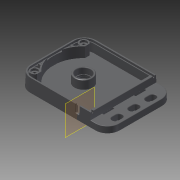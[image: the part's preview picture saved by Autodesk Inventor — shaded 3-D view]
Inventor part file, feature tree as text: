
AUTODESK INVENTOR PART (.ipt)
format: ipt  version: 2013 (Build 170138000, 138)  size: 991,744 bytes
history: native  units: mm
features: extrude x19, sketch x15, fillet x11, plane x4, hole x2, projected_geometry x1
ambient origin geometry x8: Origin, YZ Plane, XZ Plane, XY Plane, X Axis, Y Axis, Z Axis, Center Point
bodies: Solid1 (feature_tree)
feature tree (52):
  extrude  "Extrusion1"  TaperAngle=0.0deg  [1 undecoded]
  plane  "Work Plane1"
  extrude  "Extrusion2"  Depth=15.882496mm
  fillet  "Fillet1"  Radius=13.081mm
  plane  "Work Plane2"
  sketch  "Sketch5"  dims[d6=9.4996mm d7=0.0mm d8=-1.4986mm d9=8.9916mm]
  extrude  "Extrusion3"  Depth=8.9916mm
  extrude  "Extrusion4"  Depth=0.6096mm
  sketch  "Sketch9"  dims[d10=8.6614mm d12=0.6096mm d13=0.993147mm]
  sketch  "Sketch10"  dims[d14=0.6096mm d15=0.6096mm]
  extrude  "Extrusion10"  Depth=0.6096mm
  extrude  "Extrusion11"  Depth=7.668253mm
  extrude  "Extrusion12"  Depth=7.054107mm
  extrude  "Extrusion13"  Depth=6.1976mm
  hole  "Hole1"  [1 undecoded]
  plane  "Work Plane3"
  extrude  "Extrusion14"  Depth=1.9558mm TaperAngle=0.0deg
  fillet  "Fillet6"  Radius=1.4986mm
  extrude  "Extrusion15"  Depth=3.81mm
  hole  "Hole2"  [1 undecoded]
  fillet  "Fillet7"  Radius=15.809192mm
  extrude  "Extrusion17"  Depth=1.4986mm TaperAngle=0.0deg
  extrude  "Extrusion20"  Depth=1.4986mm TaperAngle=0.0deg
  extrude  "Extrusion21"  Depth=18.0594mm
  extrude  "Extrusion22"  Depth=6.5024mm
  extrude  "Extrusion23"  Depth=0.508mm
  extrude  "Extrusion24"  Depth=2.9972mm TaperAngle=0.0deg
  fillet  "Fillet10"  Radius=1.4986mm
  fillet  "Fillet11"  Radius=13.4874mm
  fillet  "Fillet12"  Radius=6.2484mm
  sketch  "Sketch22"  dims[d66=0.508mm d67=1.4986mm d68=0.0mm]
  extrude  "Extrusion25"  Depth=10.4902mm
  extrude  "Extrusion26"  Depth=4.5466mm TaperAngle=0.0deg
  fillet  "Fillet13"  Radius=9.4996mm
  fillet  "Fillet14"  Radius=4.5466mm
  fillet  "Fillet15"  Radius=2.159mm
  fillet  "Fillet16"  Radius=1.4986mm
  extrude  "Extrusion27"  Depth=0.508mm
  fillet  "Fillet17"  Radius=0.508mm
  plane  "Work Plane4"
  sketch  "Sketch1"  dims[d0=9.4996mm d1=-0.349066mm d2=0.0mm]
  sketch  "Sketch2"  dims[d3=5.0038mm d4=15.882496mm d5=13.081mm]
  projected_geometry  "Projected Loop1"
  sketch  "Sketch11"  dims[d16=7.054107mm d17=7.668253mm]
  sketch  "Sketch12"  dims[d18=8.668253mm d19=7.054107mm]
  sketch  "Sketch13"  dims[d20=1.4986mm d21=0.0mm d22=6.1976mm d23=-0.087266mm]
  sketch  "Sketch14"  dims[d36=10.6172mm d44=1.9558mm d45=0.0mm]
  sketch  "Sketch18"  dims[d46=1.9558mm d47=0.0mm d48=1.9558mm d49=0.0mm d50=1.4986mm d51=0.0mm]
  sketch  "Sketch19"  dims[d52=2.1082mm d53=19.05mm d54=9.525mm d55=6.35mm d56=14.3117mm d57=25.4mm d58=20.594885mm d59=3.81mm]
  sketch  "Sketch20"  dims[d60=8.6106mm d61=15.809192mm d62=15.809192mm]
  sketch  "Sketch21"  dims[d63=2.6162mm d64=1.4986mm d65=0.0mm]
  sketch  "Sketch23"  dims[d69=6.5024mm d70=18.0594mm d71=6.5024mm d72=3.7846mm d73=19.05mm d74=9.525mm d75=6.35mm d76=14.3117mm d77=25.4mm d78=20.594885mm d79=0.508mm d82=2.9972mm d83=0.0mm d90=1.4986mm d91=0.0mm d92=13.4874mm d93=6.2484mm d94=-0.174533mm d95=10.4902mm d96=4.5466mm d97=0.0mm d98=9.4996mm d99=4.5466mm d100=0.0mm d101=2.159mm d102=0.0mm d103=1.4986mm d104=0.508mm d105=0.508mm d106=25.4mm d107=0.0mm d108=2.6924mm d109=0.0mm d110=0.3048mm d111=0.508mm d112=0.3048mm d113=0.3048mm d114=3.7846mm d115=2.794mm d116=0.0mm d117=0.508mm]
note: 3 required parameter values undecoded (feature->parameter linkage not recoverable at this tier; creation-order binding heuristic only, values carry confidence <= 0.55)
